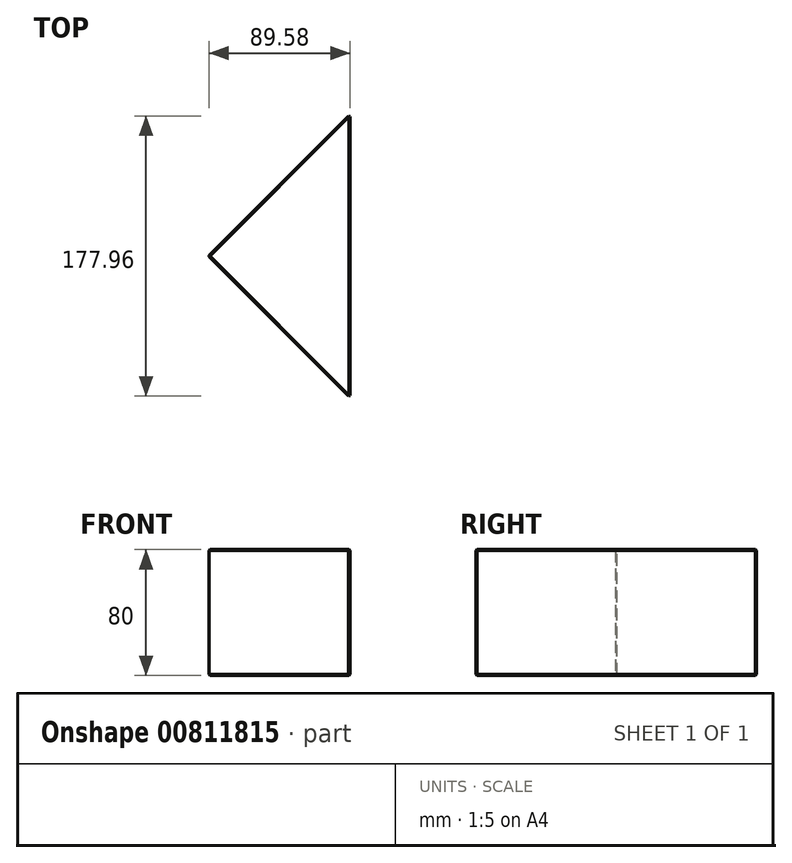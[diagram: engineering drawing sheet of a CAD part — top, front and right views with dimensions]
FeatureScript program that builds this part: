
annotation { "Feature Type Name" : "Feature", "Feature Type Description" : "" }
export const myFeature = defineFeature(function(context is Context, id is Id, definition is map)
    precondition{}
    {
        {
            var Q0;
            Q0=qCreatedBy(makeId("Top.planeOp"),FACE);
            var sketch = newSketch(context, id + "F0", { "sketchPlane" : qUnion([Q0])});
            skLineSegment(sketch, "E0.bottom", {"start": v(-90, 90) * mm, "end": v(90, 90) * mm});
            skLineSegment(sketch, "E0.top", {"start": v(-90, -90) * mm, "end": v(90, -90) * mm});
            skLineSegment(sketch, "E0.left", {"start": v(-90, 90) * mm, "end": v(-90, -90) * mm});
            skLineSegment(sketch, "E0.right", {"start": v(90, 90) * mm, "end": v(90, -90) * mm});
            skPoint(sketch, "E0.middle", {"position": v(0, 0) * mm});
            skLineSegment(sketch, "E1", {"start": v(90, 90) * mm, "end": v(0, 0) * mm});
            skLineSegment(sketch, "E2", {"start": v(0, 0) * mm, "end": v(136.8, -136.8) * mm});
            skLineSegment(sketch, "E3", {"start": v(136.8, -136.8) * mm, "end": v(308.07, 34.45) * mm});
            skLineSegment(sketch, "E4", {"start": v(308.07, 34.45) * mm, "end": v(239.24, 103.28) * mm});
            skLineSegment(sketch, "E5", {"start": v(90, 90) * mm, "end": v(127.85, 127.85) * mm});
            skLineSegment(sketch, "E6.bottom", {"start": v(-90, 90) * mm, "end": v(-12, 90) * mm});
            skLineSegment(sketch, "E6.top", {"start": v(-90, -90) * mm, "end": v(-12, -90) * mm});
            skLineSegment(sketch, "E6.right", {"start": v(-12, 90) * mm, "end": v(-12, -90) * mm});
            skSolve(sketch);
        }
        {
            var Q0;
            {var subQ0=sQuery(id+"F0.wireOp",EDGE,"E0.right");Q0=makeQuery(id+"F0.imprint","IMPRINT",FACE,{"disambiguationData":[TD([[makeQuery(id+"F0.imprint","IMPRINT",EDGE,{"derivedFrom":subQ0}),-1.0]])]});}
            var Q1;
            Q1=makeQuery(id+"F0.imprint","IMPRINT",FACE,{"disambiguationData":[TD([[makeQuery(id+"F0.imprint","IMPRINT",EDGE,{"derivedFrom":sQuery(id+"F0.wireOp",EDGE,"E6.bottom")}),-1.0]])]});
            extrude(context, id + "F1", {"entities" : qUnion([Q0, Q1]), "depth" : 80 * mm, "offsetDistance" : 25 * mm});
        }
        {
            var Q0;
            Q0=makeQuery(id+"F1.opExtrude","CAP_FACE",FACE,{"disambiguationData":[OSD([sQuery(id+"F0.wireOp",EDGE,"E6.bottom"),sQuery(id+"F0.wireOp",EDGE,"E6.top"),sQuery(id+"F0.wireOp",EDGE,"E0.left"),sQuery(id+"F0.wireOp",EDGE,"E6.right")])],"isStart":false});
            var Q1;
            Q1=makeQuery(id+"F1.opExtrude","SWEPT_FACE",FACE,{"disambiguationData":[OSD([sQuery(id+"F0.wireOp",EDGE,"E0.left")])]});
            var Q2;
            Q2=makeQuery(id+"F1.opExtrude","CAP_FACE",FACE,{"disambiguationData":[OSD([sQuery(id+"F0.wireOp",EDGE,"E6.bottom"),sQuery(id+"F0.wireOp",EDGE,"E6.top"),sQuery(id+"F0.wireOp",EDGE,"E0.left"),sQuery(id+"F0.wireOp",EDGE,"E6.right")])],"isStart":true});
            var Q3;
            Q3=makeQuery(id+"F1.opExtrude","SWEPT_FACE",FACE,{"disambiguationData":[OSD([sQuery(id+"F0.wireOp",EDGE,"E6.bottom")])]});
            var Q4;
            Q4=makeQuery(id+"F1.opExtrude","SWEPT_FACE",FACE,{"disambiguationData":[OSD([sQuery(id+"F0.wireOp",EDGE,"E6.right")])]});
            var Q5;
            Q5=makeQuery(id+"F1.opExtrude","SWEPT_FACE",FACE,{"disambiguationData":[OSD([sQuery(id+"F0.wireOp",EDGE,"E6.top")])]});
            var Q6;
            Q6=makeQuery(id+"F1.opExtrude","CAP_FACE",FACE,{"disambiguationData":[OSD([sQuery(id+"F0.wireOp",EDGE,"E0.right"),sQuery(id+"F0.wireOp",EDGE,"E1"),sQuery(id+"F0.wireOp",EDGE,"E2")])],"isStart":false});
            var Q7;
            Q7=makeQuery(id+"F1.opExtrude","SWEPT_FACE",FACE,{"disambiguationData":[OSD([sQuery(id+"F0.wireOp",EDGE,"E1")])]});
            var Q8;
            Q8=makeQuery(id+"F1.opExtrude","CAP_FACE",FACE,{"disambiguationData":[OSD([sQuery(id+"F0.wireOp",EDGE,"E0.right"),sQuery(id+"F0.wireOp",EDGE,"E1"),sQuery(id+"F0.wireOp",EDGE,"E2")])],"isStart":true});
            var Q9;
            Q9=makeQuery(id+"F1.opExtrude","SWEPT_FACE",FACE,{"disambiguationData":[OSD([sQuery(id+"F0.wireOp",EDGE,"E2")])]});
            var Q10;
            Q10=makeQuery(id+"F1.opExtrude","SWEPT_FACE",FACE,{"disambiguationData":[OSD([sQuery(id+"F0.wireOp",EDGE,"E0.right")])]});
            chamfer(context, id + "F2", {"entities" : qUnion([Q0, Q1, Q2, Q3, Q4, Q5, Q6, Q7, Q8, Q9, Q10]), "width" : 0.6 * mm, "tangentPropagation" : true});
        }
    });
